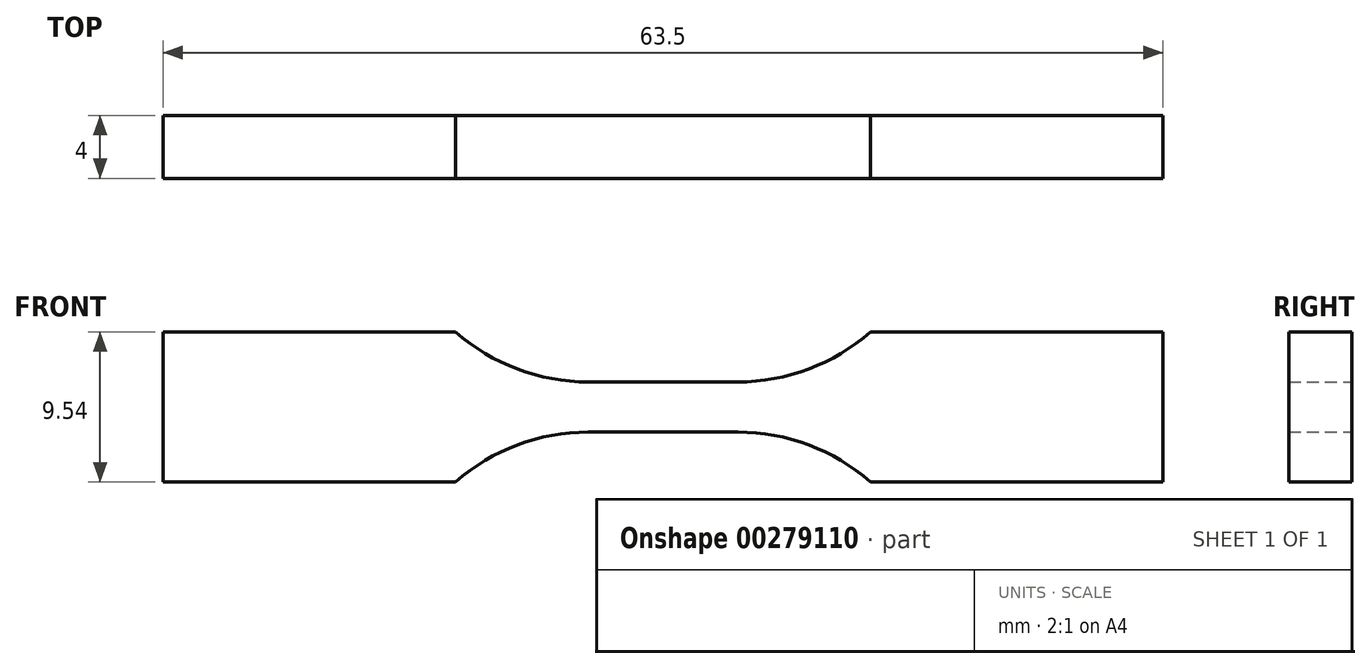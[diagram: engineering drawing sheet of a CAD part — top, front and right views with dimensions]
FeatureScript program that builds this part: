
annotation { "Feature Type Name" : "Feature", "Feature Type Description" : "" }
export const myFeature = defineFeature(function(context is Context, id is Id, definition is map)
    precondition{}
    {
        {
            var Q0;
            Q0=qCreatedBy(makeId("Front.planeOp"),FACE);
            var sketch = newSketch(context, id + "F0", { "sketchPlane" : qUnion([Q0])});
            skLineSegment(sketch, "E0", {"start": v(0, 1.59) * mm, "end": v(4.77, 1.6) * mm});
            skArc(sketch, "E1", {"start": v(4.77, 1.6) * mm, "mid": v(9.26, 2.41) * mm, "end": v(13.17, 4.77) * mm});
            skLineSegment(sketch, "E2", {"start": v(13.17, 4.77) * mm, "end": v(31.75, 4.77) * mm});
            skLineSegment(sketch, "E3", {"start": v(31.75, 4.77) * mm, "end": v(31.75, 0) * mm});
            skLineSegment(sketch, "E4.MirrorCS", {"start": v(0, -1.6) * mm, "end": v(4.77, -1.59) * mm});
            skLineSegment(sketch, "E5.MirrorCS", {"start": v(31.75, -4.77) * mm, "end": v(31.75, 0) * mm});
            skLineSegment(sketch, "E6.MirrorCS", {"start": v(13.17, -4.77) * mm, "end": v(31.75, -4.77) * mm});
            skArc(sketch, "E7.MirrorCS", {"start": v(4.77, -1.6) * mm, "mid": v(9.26, -2.41) * mm, "end": v(13.17, -4.77) * mm});
            skLineSegment(sketch, "E8.MirrorCS", {"start": v(-31.75, -4.77) * mm, "end": v(-31.75, 0) * mm});
            skLineSegment(sketch, "E9.MirrorCS", {"start": v(-13.17, 4.77) * mm, "end": v(-31.75, 4.76) * mm});
            skLineSegment(sketch, "E10.MirrorCS", {"start": v(0, 1.6) * mm, "end": v(-4.77, 1.59) * mm});
            skLineSegment(sketch, "E11.MirrorCS", {"start": v(-31.75, 4.77) * mm, "end": v(-31.75, 0) * mm});
            skArc(sketch, "E12.MirrorCS", {"start": v(-4.77, -1.6) * mm, "mid": v(-9.26, -2.41) * mm, "end": v(-13.17, -4.77) * mm});
            skArc(sketch, "E13.MirrorCS", {"start": v(-4.77, 1.6) * mm, "mid": v(-9.26, 2.41) * mm, "end": v(-13.17, 4.77) * mm});
            skLineSegment(sketch, "E14.MirrorCS", {"start": v(-13.17, -4.77) * mm, "end": v(-31.75, -4.77) * mm});
            skLineSegment(sketch, "E15.MirrorCS", {"start": v(0, -1.59) * mm, "end": v(-4.77, -1.6) * mm});
            skSolve(sketch);
        }
        {
            var Q0;
            Q0=makeQuery(id+"F0.imprint","IMPRINT",FACE,{"disambiguationData":[TD([[makeQuery(id+"F0.imprint","IMPRINT",EDGE,{"derivedFrom":sQuery(id+"F0.wireOp",EDGE,"E3")}),-1.0]])]});
            extrude(context, id + "F1", {"entities" : qUnion([Q0]), "endBound" : BoundingType.SYMMETRIC, "depth" : 4 * mm});
        }
    });
